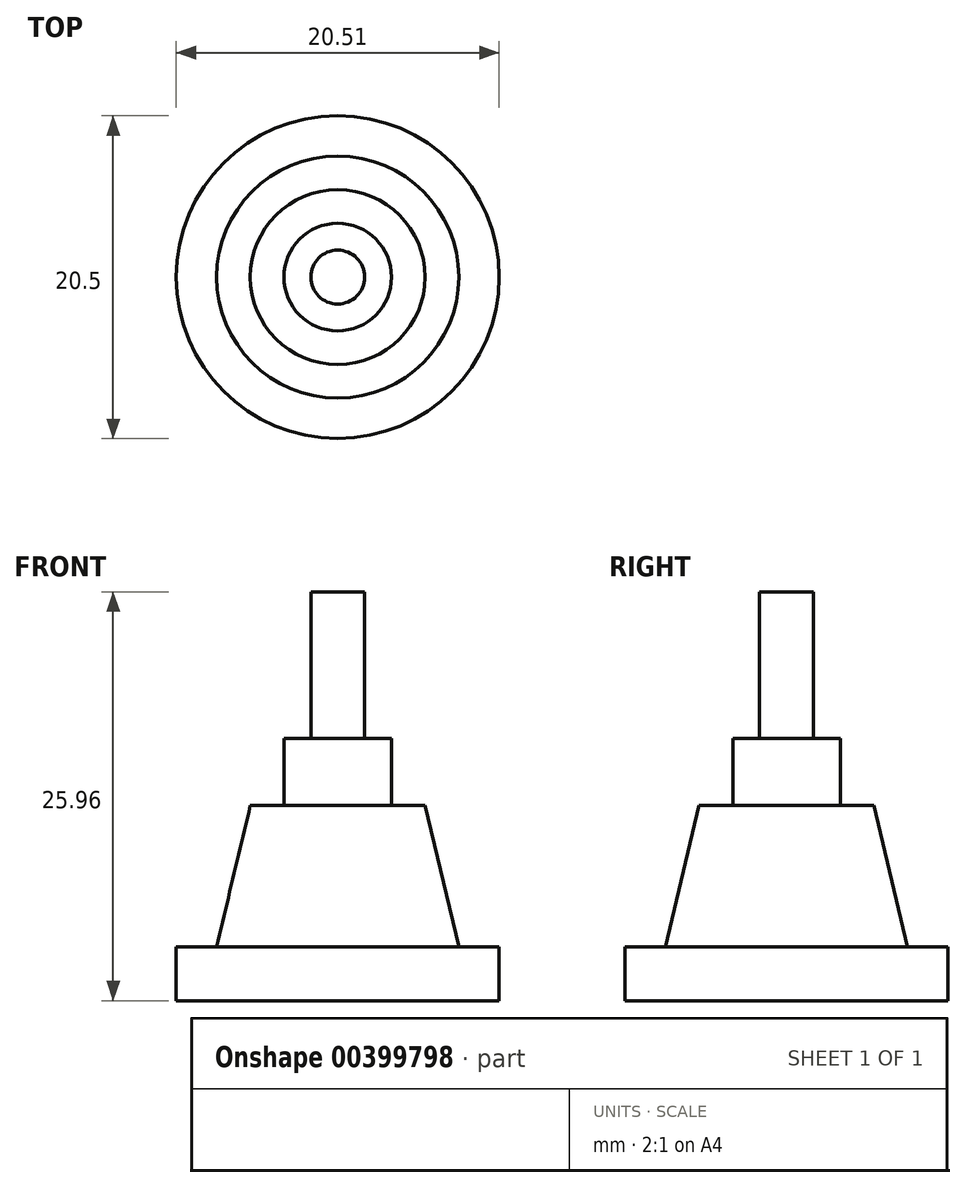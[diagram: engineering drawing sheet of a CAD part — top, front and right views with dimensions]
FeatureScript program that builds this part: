
annotation { "Feature Type Name" : "Feature", "Feature Type Description" : "" }
export const myFeature = defineFeature(function(context is Context, id is Id, definition is map)
    precondition{}
    {
        {
            var Q0;
            Q0=qCreatedBy(makeId("Front.planeOp"),FACE);
            var sketch = newSketch(context, id + "F0", { "sketchPlane" : qUnion([Q0])});
            skLineSegment(sketch, "E0", {"start": v(-39.31, -25.96) * mm, "end": v(-39.31, -22.54) * mm});
            skLineSegment(sketch, "E1", {"start": v(-39.31, -22.54) * mm, "end": v(-36.75, -22.54) * mm});
            skLineSegment(sketch, "E2", {"start": v(-36.75, -22.54) * mm, "end": v(-34.61, -13.57) * mm});
            skLineSegment(sketch, "E3", {"start": v(-34.61, -13.57) * mm, "end": v(-32.47, -13.57) * mm});
            skLineSegment(sketch, "E4", {"start": v(-32.47, -13.57) * mm, "end": v(-32.47, -9.3) * mm});
            skLineSegment(sketch, "E5", {"start": v(-32.47, -9.3) * mm, "end": v(-30.76, -9.3) * mm});
            skLineSegment(sketch, "E6", {"start": v(-30.76, -9.3) * mm, "end": v(-30.76, 0) * mm});
            skLineSegment(sketch, "E7", {"start": v(-30.76, 0) * mm, "end": v(-29.06, 0) * mm});
            skLineSegment(sketch, "E8", {"start": v(-39.31, -25.96) * mm, "end": v(-29.06, -25.96) * mm});
            skLineSegment(sketch, "E9", {"start": v(-29.06, -25.96) * mm, "end": v(-29.06, 0) * mm});
            skSolve(sketch);
        }
        {
            var Q0;
            Q0=makeQuery(id+"F0.imprint","IMPRINT",FACE,{"disambiguationData":[TD([[makeQuery(id+"F0.imprint","IMPRINT",EDGE,{"derivedFrom":sQuery(id+"F0.wireOp",EDGE,"E0")}),-1.0]])]});
            var Q1;
            Q1=sQuery(id+"F0.wireOp",EDGE,"E8");
            var Q2;
            Q2=sQuery(id+"F0.wireOp",EDGE,"E6");
            var Q3;
            Q3=sQuery(id+"F0.wireOp",EDGE,"E2");
            var Q4;
            Q4=sQuery(id+"F0.wireOp",EDGE,"E7");
            var Q5;
            Q5=sQuery(id+"F0.wireOp",EDGE,"E4");
            var Q6;
            Q6=sQuery(id+"F0.wireOp",EDGE,"E5");
            var Q7;
            Q7=sQuery(id+"F0.wireOp",EDGE,"E3");
            var Q8;
            Q8=sQuery(id+"F0.wireOp",EDGE,"E1");
            var Q9;
            Q9=sQuery(id+"F0.wireOp",EDGE,"E0");
            var Q10;
            Q10=sQuery(id+"F0.wireOp",EDGE,"E9");
            revolve(context, id + "F1", {"entities" : qUnion([Q0]), "surfaceEntities" : qUnion([Q1, Q2, Q3, Q4, Q5, Q6, Q7, Q8, Q9]), "axis" : qUnion([Q10]), "revolveType" : RevolveType.FULL});
        }
    });
